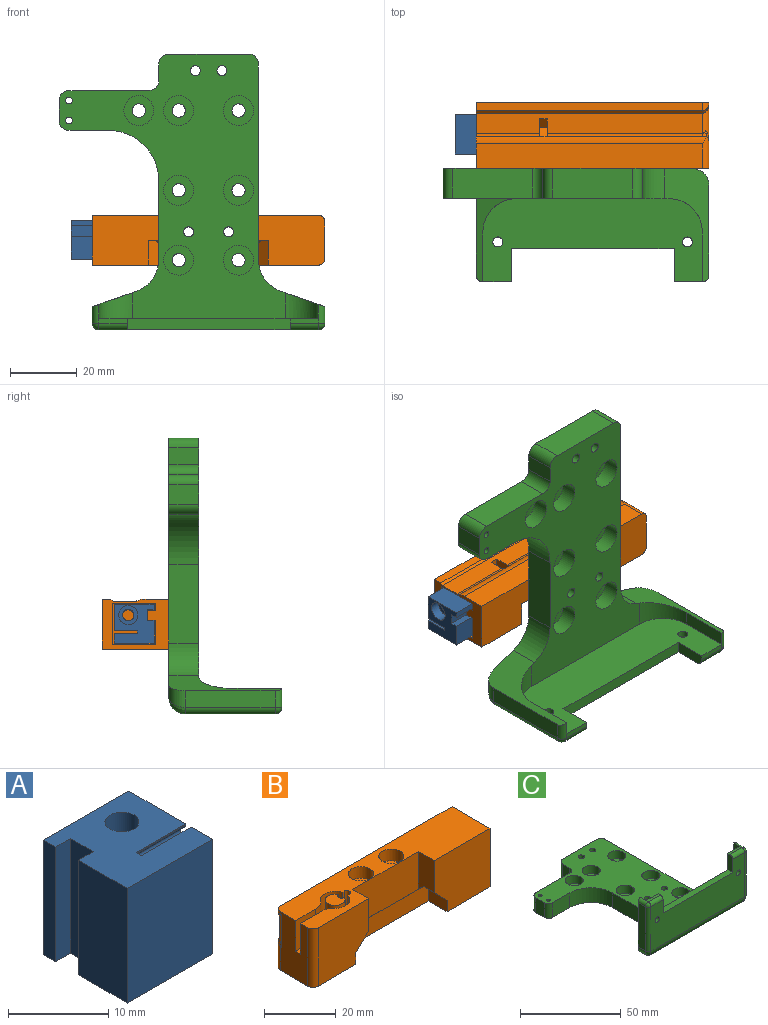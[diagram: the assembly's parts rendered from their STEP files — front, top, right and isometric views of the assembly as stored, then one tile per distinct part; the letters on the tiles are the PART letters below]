
ASSEMBLY  parts=3 mates=4
PART A: 45 faces, bbox 12x11.8x14 mm
  f0: plane 7x0mm, normal (0,-1,0), area 0mm2, adj f7,f19,f31,f34
  f1: plane 7x0mm, normal (0,-1,0), area 0mm2, adj f7,f19,f33,f36
  f2: plane 7x0mm, normal (0,-1,0), area 0mm2, adj f7,f19,f35,f38
  f3: plane 7x0mm, normal (0,-1,0), area 0mm2, adj f7,f19,f37,f40
  f4: plane 7x0mm, normal (0,-1,0), area 0mm2, adj f7,f19,f39,f42
  f5: plane 7x0mm, normal (0,-1,0), area 0mm2, adj f7,f19,f41,f44
  f6: plane 7x0.21mm, normal (0,-1,0), area 1.4mm2, adj f7,f19,f21,f43
  f7: plane 14x8.04mm, normal (1,0,0), area 107.1mm2, adj f0,f1,f2,f3,f4,f5,f6,f9
  f8: cylinder r=1.7mm len=11mm, axis (0,0,-1), area 117.5mm2, adj f20,f23
  f9: plane 7x0.15mm, normal (0,-1,0), area 1mm2, adj f7,f19,f20,f32
  f10: plane 14x12mm, normal (0,1,0), area 168mm2, adj f7,f11,f20,f21
  f11: plane 14x1.7mm, normal (-1,0,0), area 23.8mm2, adj f10,f12,f20,f21
  f12: plane 14x2.1mm, normal (0,-1,0), area 29.4mm2, adj f11,f13,f20,f21
  f13: plane 14x3.21mm, normal (-1,0,0), area 44.9mm2, adj f12,f14,f20,f21
  f14: plane 14x2.1mm, normal (0,1,0), area 29.4mm2, adj f13,f15,f20,f21
  f15: plane 14x6.89mm, normal (-1,0,0), area 96.5mm2, adj f14,f16,f20,f21
  f16: plane 14x12mm, normal (0,-1,0), area 168mm2, adj f15,f17,f20,f21
  f17: plane 14x3mm, normal (1,0,0), area 42mm2, adj f16,f18,f20,f21
  f18: plane 14x7mm, normal (0,1,0), area 98mm2, adj f17,f19,f20,f21
  f19: plane 14x1.53mm, normal (1,0,0), area 16.1mm2, adj f0,f1,f2,f3,f4,f5,f6,f9
  f20: plane 12x11.8mm, normal (0,0,1), area 120.5mm2, adj f7,f8,f9,f10,f11,f12,f13,f14
  f21: plane 12x11.8mm, normal (0,0,-1), area 103.5mm2, adj f6,f7,f10,f11,f12,f13,f14,f15
  f22: cylinder r=2.88mm len=5.76mm, axis (0,0,-1), area 54.3mm2, adj f21,f23
  f23: plane 5.76x5.76mm, normal (0,0,-1), area 17mm2, adj f8,f22
  f24: cylinder r=0.55mm len=7mm, axis (1,0,0), area 10.3mm2, adj f7,f19,f43,f44
  f25: cylinder r=0.55mm len=7mm, axis (1,0,0), area 10.3mm2, adj f7,f19,f41,f42
  f26: cylinder r=0.55mm len=7mm, axis (1,0,0), area 10.3mm2, adj f7,f19,f39,f40
  f27: cylinder r=0.55mm len=7mm, axis (1,0,0), area 10.3mm2, adj f7,f19,f37,f38
  f28: cylinder r=0.55mm len=7mm, axis (1,0,0), area 10.3mm2, adj f7,f19,f35,f36
  f29: cylinder r=0.55mm len=7mm, axis (1,0,0), area 10.3mm2, adj f7,f19,f33,f34
  f30: cylinder r=0.55mm len=7mm, axis (1,0,0), area 10.3mm2, adj f7,f19,f31,f32
  f31: cylinder r=0.45mm len=7mm, axis (1,0,0), area 4.2mm2, adj f0,f7,f19,f30
  f32: cylinder r=0.45mm len=7mm, axis (1,0,0), area 4.2mm2, adj f7,f9,f19,f30
  f33: cylinder r=0.45mm len=7mm, axis (1,0,0), area 4.2mm2, adj f1,f7,f19,f29
  f34: cylinder r=0.45mm len=7mm, axis (1,0,0), area 4.2mm2, adj f0,f7,f19,f29
  f35: cylinder r=0.45mm len=7mm, axis (1,0,0), area 4.2mm2, adj f2,f7,f19,f28
  f36: cylinder r=0.45mm len=7mm, axis (1,0,0), area 4.2mm2, adj f1,f7,f19,f28
  f37: cylinder r=0.45mm len=7mm, axis (1,0,0), area 4.2mm2, adj f3,f7,f19,f27
  f38: cylinder r=0.45mm len=7mm, axis (1,0,0), area 4.2mm2, adj f2,f7,f19,f27
  f39: cylinder r=0.45mm len=7mm, axis (1,0,0), area 4.2mm2, adj f4,f7,f19,f26
  f40: cylinder r=0.45mm len=7mm, axis (1,0,0), area 4.2mm2, adj f3,f7,f19,f26
  f41: cylinder r=0.45mm len=7mm, axis (1,0,0), area 4.2mm2, adj f5,f7,f19,f25
  f42: cylinder r=0.45mm len=7mm, axis (1,0,0), area 4.2mm2, adj f4,f7,f19,f25
  f43: cylinder r=0.45mm len=7mm, axis (1,0,0), area 4.2mm2, adj f6,f7,f19,f24
  f44: cylinder r=0.45mm len=7mm, axis (1,0,0), area 4.2mm2, adj f5,f7,f19,f24
PART B: 75 faces, bbox 70.3x15.9x20 mm
  f0: plane 12.9x6.3mm, normal (1,0,0), area 71.1mm2, adj f1,f9,f13,f73,f74
  f1: plane 26x12.9mm, normal (0,-1,0), area 335.4mm2, adj f0,f2,f9,f74
  f2: plane 12.9x6.3mm, normal (-1,0,0), area 71.1mm2, adj f1,f9,f10,f72,f74
  f3: plane 68x7.45mm, normal (0,1,0), area 506.5mm2, adj f11,f14,f54,f61
  f4: plane 20x11mm, normal (-1,0,0), area 192mm2, adj f9,f14,f15,f16,f17,f54,f55,f56
  f5: plane 8.54x5.41mm, normal (-1,0,0), area 29.1mm2, adj f47,f48,f49,f52,f61,f65,f67,f68
  f6: plane 8.54x5.41mm, normal (1,0,0), area 29.1mm2, adj f48,f49,f51,f52,f61,f62,f67,f68
  f7: cylinder r=2mm len=16mm, axis (0,0,-1), area 201.1mm2, adj f14,f37
  f8: cylinder r=2mm len=16mm, axis (0,0,-1), area 201.1mm2, adj f14,f35
  f9: plane 70x15mm, normal (0,0,1), area 728.2mm2, adj f0,f1,f2,f4,f10,f11,f12,f13
  f10: plane 22x20mm, normal (0,-1,0), area 407.5mm2, adj f2,f9,f11,f14,f70,f72
  f11: plane 20x15mm, normal (1,0,0), area 138.2mm2, adj f3,f9,f10,f12,f14,f38,f39,f40
  f12: plane 68x2.6mm, normal (0,1,0), area 176.8mm2, adj f9,f11,f56,f59
  f13: plane 20x20mm, normal (0,-1,0), area 367.5mm2, adj f0,f9,f14,f66,f69,f73
  f14: plane 70x15mm, normal (0,0,-1), area 756.8mm2, adj f3,f4,f7,f8,f10,f11,f13,f54
  f15: plane 10.5x8.31mm, normal (0,1,0), area 87.3mm2, adj f4,f9,f17,f22
  f16: plane 10.5x7.88mm, normal (0,-1,0), area 82.7mm2, adj f4,f9,f17,f21
  f17: plane 19.12x8.24mm, normal (0,0,1), area 32.1mm2, adj f4,f15,f16,f18,f21,f22,f53
  f18: cylinder r=4.12mm len=10.5mm, axis (0,0,1), area 193.1mm2, adj f9,f17,f21,f22,f26,f27,f28
  f19: cylinder r=2.75mm len=9.5mm, axis (0,0,1), area 146.8mm2, adj f20,f24,f25,f31,f53
  f20: plane 5.5x5.31mm, normal (0,0,1), area 21.8mm2, adj f19,f23,f25,f30,f31
  f21: cylinder r=5mm len=10.5mm, axis (0,0,1), area 47mm2, adj f9,f16,f17,f18
  f22: cylinder r=5mm len=10.5mm, axis (0,0,1), area 43.2mm2, adj f9,f15,f17,f18
  f23: plane 8x0.12mm, normal (1,0,0), area 0.9mm2, adj f20,f24,f30,f31
  f24: plane 2.12x1.2mm, normal (0,0,1), area 2mm2, adj f19,f23,f25,f30,f31
  f25: plane 8x0.01mm, normal (0,1,0), area 0.1mm2, adj f19,f20,f24,f30
  f26: plane 2.12x1.74mm, normal (0,0,1), area 3mm2, adj f18,f27,f28,f29,f32,f33
  f27: plane 8x0.71mm, normal (0,1,0), area 5.7mm2, adj f9,f18,f26,f32
  f28: plane 8x0.74mm, normal (0,-1,0), area 5.9mm2, adj f9,f18,f26,f33
  f29: plane 8x0.12mm, normal (-1,0,0), area 0.9mm2, adj f9,f26,f32,f33
  f30: cylinder r=1mm len=8mm, axis (0,0,-1), area 12.6mm2, adj f20,f23,f24,f25
  f31: cylinder r=1mm len=8mm, axis (0,0,1), area 12.3mm2, adj f19,f20,f23,f24
  f32: cylinder r=1mm len=8mm, axis (0,0,1), area 12.6mm2, adj f9,f26,f27,f29
  f33: cylinder r=1mm len=8mm, axis (0,0,-1), area 12.6mm2, adj f9,f26,f28,f29
  f34: cylinder r=3.5mm len=7mm, axis (0,0,1), area 88mm2, adj f9,f35
  f35: plane 7x7mm, normal (0,0,1), area 25.9mm2, adj f8,f34
  f36: cylinder r=3.5mm len=7mm, axis (0,0,1), area 88mm2, adj f9,f37
  f37: plane 7x7mm, normal (0,0,1), area 25.9mm2, adj f7,f36
  f38: plane 14x2.5mm, normal (0,-1,0), area 35mm2, adj f11,f39,f45,f46
  f39: plane 14x3mm, normal (0,0,1), area 42mm2, adj f11,f38,f40,f46
  f40: plane 14x2.5mm, normal (0,1,0), area 35mm2, adj f11,f39,f41,f46
  f41: plane 14x2.2mm, normal (0,0,1), area 30.8mm2, adj f11,f40,f42,f46
  f42: plane 14x13mm, normal (0,-1,0), area 182mm2, adj f11,f41,f43,f46
  f43: plane 14x12.6mm, normal (0,0,-1), area 176.4mm2, adj f11,f42,f44,f46
  f44: plane 14x13mm, normal (0,1,0), area 182mm2, adj f11,f43,f45,f46
  f45: plane 14x7.4mm, normal (0,0,1), area 103.6mm2, adj f11,f38,f44,f46
  f46: plane 13x12.6mm, normal (1,0,0), area 147.7mm2, adj f38,f39,f40,f41,f42,f43,f44,f45
  f47: cylinder r=1.65mm len=5mm, axis (1,0,0), area 51.8mm2, adj f5,f46
  f48: plane 5.84x2.35mm, normal (0,0,1), area 13.7mm2, adj f5,f6,f61,f68
  f49: plane 5.6x2.35mm, normal (0,0,-1), area 13.2mm2, adj f5,f6,f52,f67
  f50: plane 3.3x3.3mm, normal (1,0,0), area 8.6mm2, adj f51
  f51: cylinder r=1.65mm len=5.35mm, axis (1,0,0), area 55.5mm2, adj f6,f50
  f52: plane 68x6.2mm, normal (0,1,0), area 411.1mm2, adj f5,f6,f11,f49,f57,f59,f62,f65
  f53: torus R=3.75mm, axis (0,0,-1), area 30.7mm2, adj f17,f19
  f54: cylinder r=2mm len=9.64mm, axis (0,0,1), area 27.3mm2, adj f3,f4,f14,f55,f61,f64
  f55: cylinder r=2mm len=1.4mm, axis (0,1,0), area 0.3mm2, adj f4,f54,f64
  f56: cylinder r=2mm len=2.6mm, axis (0,0,1), area 5.4mm2, adj f4,f9,f12,f58,f60
  f57: cylinder r=2mm len=11.5mm, axis (0,0,-1), area 25mm2, adj f4,f52,f60,f63,f64
  f58: cylinder r=2mm len=2.45mm, axis (0,-1,0), area 0.7mm2, adj f4,f56,f60
  f59: plane 68x0.7mm, normal (0,0.71,-0.71), area 67.3mm2, adj f11,f12,f52,f60
  f60: bspline ~2.84x2.84mm, area 1.9mm2, adj f56,f57,f58,f59
  f61: cylinder r=5mm len=69.33mm, axis (1,0,0), area 154.8mm2, adj f3,f5,f6,f11,f48,f54,f62,f63
  f62: cylinder r=2mm len=46.65mm, axis (1,0,0), area 42.1mm2, adj f6,f52,f61,f63
  f63: bspline ~2.59x2.02mm, area 1.5mm2, adj f57,f61,f62,f64
  f64: bspline ~3.59x3.59mm, area 3.1mm2, adj f54,f55,f57,f61,f63
  f65: cylinder r=2mm len=19mm, axis (1,0,0), area 17.1mm2, adj f5,f11,f52,f61
  f66: cylinder r=2mm len=20mm, axis (0,0,-1), area 62.8mm2, adj f4,f9,f13,f14
  f67: plane 2.71x2.71mm, normal (0,0.71,-0.71), area 9mm2, adj f5,f6,f49,f68
  f68: plane 2.71x2.71mm, normal (0,0.71,0.71), area 9mm2, adj f5,f6,f48,f67
  f69: plane 7.4x4mm, normal (1,0,0), area 29.6mm2, adj f13,f14,f71,f73
  f70: plane 7.4x4mm, normal (-1,0,0), area 29.6mm2, adj f10,f14,f71,f72
  f71: plane 36x6mm, normal (0,-1,0), area 212mm2, adj f14,f69,f70,f72,f73,f74
  f72: plane 7.4x5mm, normal (-0.71,0,-0.71), area 46mm2, adj f2,f10,f70,f71,f74
  f73: plane 7.4x5mm, normal (0.71,0,-0.71), area 46mm2, adj f0,f13,f69,f71,f74
  f74: plane 32x3mm, normal (0,-0.71,-0.71), area 53.2mm2, adj f0,f1,f2,f71,f72,f73
PART C: 74 faces, bbox 80x83x34 mm
  f0: cylinder r=2mm len=4mm, axis (0,0,-1), area 50.3mm2, adj f28,f72
  f1: cylinder r=2mm len=4mm, axis (0,0,-1), area 50.3mm2, adj f28,f70
  f2: cylinder r=2mm len=4mm, axis (0,0,-1), area 50.3mm2, adj f28,f68
  f3: cylinder r=2mm len=4mm, axis (0,0,-1), area 50.3mm2, adj f28,f66
  f4: cylinder r=2mm len=4mm, axis (0,0,-1), area 50.3mm2, adj f28,f64
  f5: cylinder r=2mm len=4mm, axis (0,0,-1), area 50.3mm2, adj f28,f62
  f6: cylinder r=2mm len=4mm, axis (0,0,-1), area 50.3mm2, adj f28,f60
  f7: plane 49x3.5mm, normal (0,0,1), area 171.5mm2, adj f8,f13,f38,f40
  f8: plane 66x25mm, normal (0,1,0), area 1102.9mm2, adj f7,f9,f34,f35,f36,f37,f38,f39
  f9: plane 79.5x68mm, normal (0,0,1), area 2471.7mm2, adj f8,f10,f11,f15,f16,f17,f18,f19
  f10: plane 23.91x9mm, normal (-1,0,0), area 215.1mm2, adj f9,f28,f53,f73
  f11: plane 34x13.3mm, normal (-0.33,0.94,0), area 196mm2, adj f9,f12,f28,f34,f37,f51,f53,f54
  f12: plane 27x5mm, normal (-1,0,0), area 135mm2, adj f11,f49,f51,f54
  f13: plane 66x27mm, normal (0,-1,0), area 1375.9mm2, adj f7,f38,f40,f42,f43,f44,f45,f48
  f14: plane 27x5mm, normal (1,0,0), area 135mm2, adj f15,f44,f47,f58
  f15: plane 34x13.3mm, normal (0.33,0.94,0), area 196mm2, adj f9,f14,f28,f35,f36,f47,f52,f58
  f16: plane 58.91x9mm, normal (1,0,0), area 530.1mm2, adj f9,f28,f29,f52
  f17: plane 24x9mm, normal (0,1,0), area 216mm2, adj f9,f28,f29,f30
  f18: plane 9x5mm, normal (-1,0,0), area 45mm2, adj f9,f28,f30,f31
  f19: plane 24x9mm, normal (0,1,0), area 216mm2, adj f9,f28,f31,f32
  f20: plane 9x6mm, normal (-1,0,0), area 54mm2, adj f9,f28,f32,f33
  f21: cylinder r=1.5mm len=9mm, axis (0,0,-1), area 84.8mm2, adj f9,f28
  f22: cylinder r=1.5mm len=9mm, axis (0,0,-1), area 84.8mm2, adj f9,f28
  f23: cylinder r=1.5mm len=9mm, axis (0,0,-1), area 84.8mm2, adj f9,f28
  f24: cylinder r=1.5mm len=9mm, axis (0,0,-1), area 84.8mm2, adj f9,f28
  f25: cylinder r=1mm len=9mm, axis (0,0,-1), area 56.5mm2, adj f9,f28
  f26: cylinder r=1mm len=9mm, axis (0,0,-1), area 56.5mm2, adj f9,f28
  f27: plane 12x9mm, normal (0,-1,0), area 108mm2, adj f9,f28,f33,f73
  f28: plane 78x75mm, normal (0,0,-1), area 2829.7mm2, adj f0,f1,f2,f3,f4,f5,f6,f10
  f29: cylinder r=3mm len=9mm, axis (0,0,-1), area 42.4mm2, adj f9,f16,f17,f28
  f30: cylinder r=3mm len=9mm, axis (0,0,1), area 42.4mm2, adj f9,f17,f18,f28
  f31: cylinder r=3mm len=9mm, axis (0,0,1), area 42.4mm2, adj f9,f18,f19,f28
  f32: cylinder r=3mm len=9mm, axis (0,0,-1), area 42.4mm2, adj f9,f19,f20,f28
  f33: cylinder r=3mm len=9mm, axis (0,0,1), area 42.4mm2, adj f9,f20,f27,f28
  f34: plane 15x4.2mm, normal (1,0,0), area 63mm2, adj f8,f11,f37,f51
  f35: plane 15x4.2mm, normal (-1,0,0), area 63mm2, adj f8,f15,f36,f47
  f36: cylinder r=10mm len=10mm, axis (0,-1,0), area 86mm2, adj f8,f9,f15,f35
  f37: cylinder r=10mm len=10mm, axis (0,1,0), area 86mm2, adj f8,f9,f11,f34
  f38: plane 10x3.5mm, normal (1,0,0), area 34.1mm2, adj f7,f8,f13,f39,f48
  f39: plane 8.5x1.5mm, normal (0,0,1), area 12.8mm2, adj f8,f38,f48,f51
  f40: plane 10x3.5mm, normal (-1,0,0), area 34.1mm2, adj f7,f8,f13,f41,f45
  f41: plane 8.5x1.5mm, normal (0,0,1), area 12.8mm2, adj f8,f40,f45,f47
  f42: cylinder r=1.5mm len=3.5mm, axis (0,1,0), area 33mm2, adj f8,f13
  f43: cylinder r=1.5mm len=3.5mm, axis (0,1,0), area 33mm2, adj f8,f13
  f44: cylinder r=2mm len=27mm, axis (0,0,-1), area 84.8mm2, adj f13,f14,f46,f57
  f45: cylinder r=2mm len=8.5mm, axis (-1,0,0), area 26.7mm2, adj f13,f40,f41,f46
  f46: sphere r=2mm, area 6.3mm2, adj f44,f45,f47
  f47: cylinder r=2mm len=5.7mm, axis (0,-1,0), area 16.5mm2, adj f14,f15,f35,f41,f46
  f48: cylinder r=2mm len=8.5mm, axis (-1,0,0), area 26.7mm2, adj f13,f38,f39,f50
  f49: cylinder r=2mm len=27mm, axis (0,0,-1), area 84.8mm2, adj f12,f13,f50,f55
  f50: sphere r=2mm, area 6.3mm2, adj f48,f49,f51
  f51: cylinder r=2mm len=5.7mm, axis (0,1,0), area 16.5mm2, adj f11,f12,f34,f39,f50
  f52: cylinder r=10mm len=9.44mm, axis (0,0,1), area 111.1mm2, adj f9,f15,f16,f28
  f53: cylinder r=10mm len=9.44mm, axis (0,0,-1), area 111.1mm2, adj f9,f10,f11,f28
  f54: cylinder r=5mm len=6.75mm, axis (0,-1,0), area 35.7mm2, adj f11,f12,f28,f55
  f55: bspline ~5.91x5mm, area 16.7mm2, adj f49,f54,f56
  f56: cylinder r=5mm len=66mm, axis (1,0,0), area 501.2mm2, adj f13,f28,f55,f57
  f57: bspline ~5.91x5mm, area 16.7mm2, adj f44,f56,f58
  f58: cylinder r=5mm len=6.75mm, axis (0,1,0), area 35.7mm2, adj f14,f15,f28,f57
  f59: cylinder r=4.5mm len=9mm, axis (0,0,1), area 141.4mm2, adj f9,f60
  f60: plane 9x9mm, normal (0,0,1), area 51.1mm2, adj f6,f59
  f61: cylinder r=4.5mm len=9mm, axis (0,0,1), area 141.4mm2, adj f9,f62
  f62: plane 9x9mm, normal (0,0,1), area 51.1mm2, adj f5,f61
  f63: cylinder r=4.5mm len=9mm, axis (0,0,1), area 141.4mm2, adj f9,f64
  f64: plane 9x9mm, normal (0,0,1), area 51.1mm2, adj f4,f63
  f65: cylinder r=4.5mm len=9mm, axis (0,0,1), area 141.4mm2, adj f9,f66
  f66: plane 9x9mm, normal (0,0,1), area 51.1mm2, adj f3,f65
  f67: cylinder r=4.5mm len=9mm, axis (0,0,1), area 141.4mm2, adj f9,f68
  f68: plane 9x9mm, normal (0,0,1), area 51.1mm2, adj f2,f67
  f69: cylinder r=4.5mm len=9mm, axis (0,0,1), area 141.4mm2, adj f9,f70
  f70: plane 9x9mm, normal (0,0,1), area 51.1mm2, adj f1,f69
  f71: cylinder r=4.5mm len=9mm, axis (0,0,1), area 141.4mm2, adj f9,f72
  f72: plane 9x9mm, normal (0,0,1), area 51.1mm2, adj f0,f71
  f73: cylinder r=15mm len=15mm, axis (0,0,-1), area 212.1mm2, adj f9,f10,f27,f28
PLACE A rot(axis=(0.58,0.58,0.58),120deg) t=(-39.15,20.72,-26.46)mm
PLACE B rot(axis=(0,0.71,0.71),180deg) t=(8.21,16.32,-18.22)mm
PLACE C rot(axis=(1,0,0),90deg) t=(-12.79,16.32,-47.72)mm fixed
MATE cylindrical B.f7 <-> C.f22  axis (0,1,0) through (8.21,32.32,-18.22)mm
MATE cylindrical B.f8 <-> C.f21  axis (0,1,0) through (-3.79,36.32,-18.22)mm
MATE planar A.f14 <-> B.f38  axis (0,0,1) through (-32.15,21.77,-19.57)mm
MATE planar A.f13 <-> B.f39  axis (0,-1,0) through (-32.15,22.82,-17.97)mm
